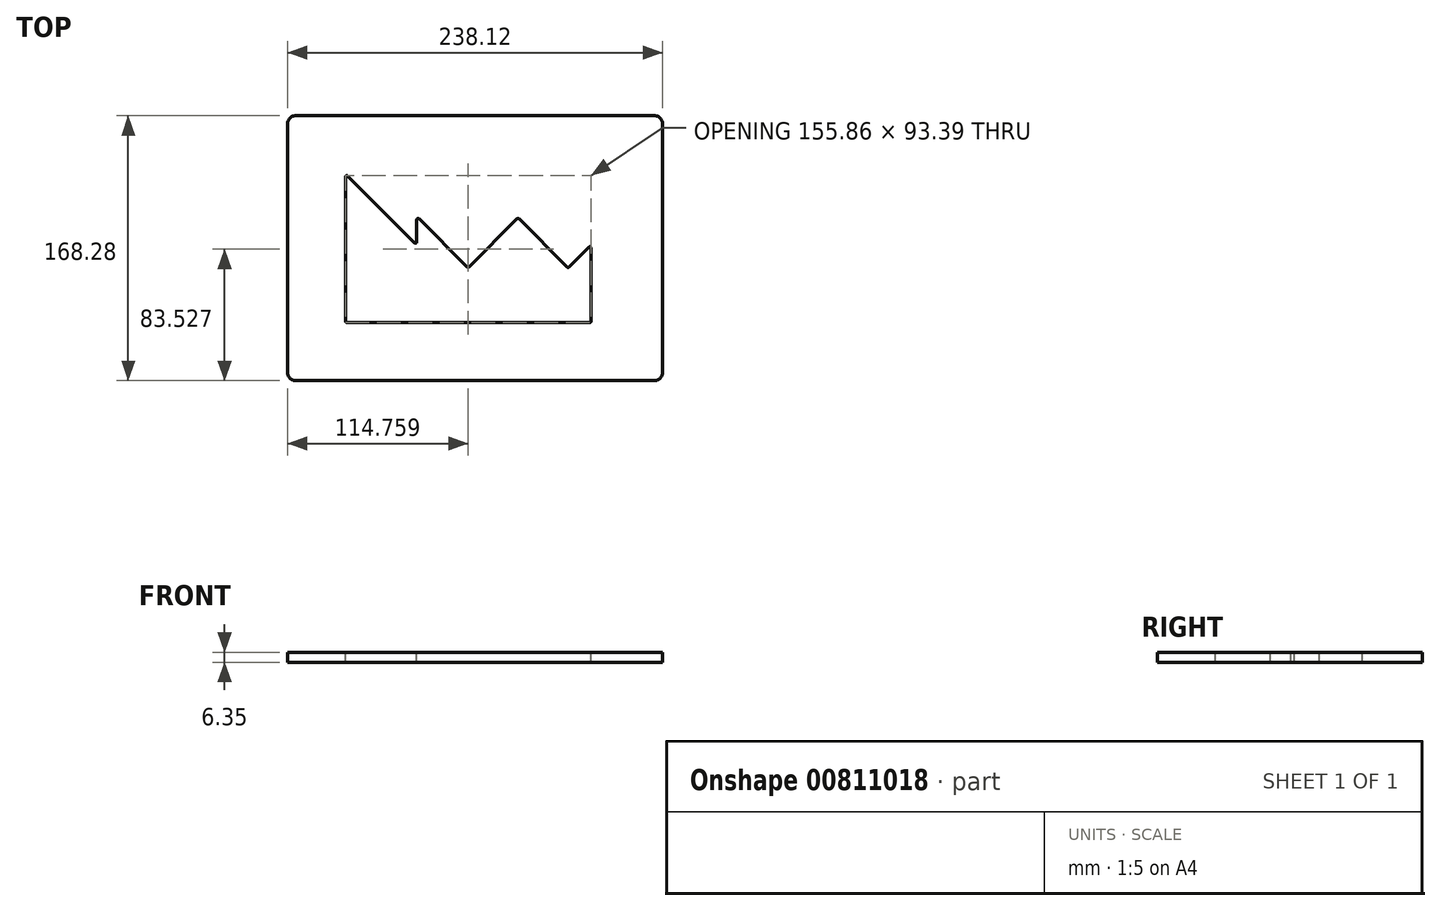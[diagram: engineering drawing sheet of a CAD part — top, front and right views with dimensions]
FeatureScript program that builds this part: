
annotation { "Feature Type Name" : "Feature", "Feature Type Description" : "" }
export const myFeature = defineFeature(function(context is Context, id is Id, definition is map)
    precondition{}
    {
        {
            var Q0;
            Q0=qCreatedBy(makeId("Top.planeOp"),FACE);
            var sketch = newSketch(context, id + "F0", { "sketchPlane" : qUnion([Q0])});
            skLineSegment(sketch, "E0.bottom", {"start": v(119.06, 84.14) * mm, "end": v(-119.06, 84.14) * mm});
            skLineSegment(sketch, "E0.top", {"start": v(119.06, -84.14) * mm, "end": v(-119.06, -84.14) * mm});
            skLineSegment(sketch, "E0.left", {"start": v(119.06, 84.14) * mm, "end": v(119.06, -84.14) * mm});
            skLineSegment(sketch, "E0.right", {"start": v(-119.06, 84.14) * mm, "end": v(-119.06, -84.14) * mm});
            skPoint(sketch, "E0.middle", {"position": v(0, 0) * mm});
            skSolve(sketch);
        }
        {
            var Q0;
            Q0 = qSketchRegion(id + "F0", true);
            extrude(context, id + "F1", {"entities" : qUnion([Q0]), "depth" : 6.35 * mm, "offsetDistance" : 25.4 * mm});
        }
        {
            var Q0;
            Q0=makeQuery(id+"F1.opExtrude","CAP_FACE",FACE,{"disambiguationData":[OSD([sQuery(id+"F0.wireOp",EDGE,"E0.bottom"),sQuery(id+"F0.wireOp",EDGE,"E0.top"),sQuery(id+"F0.wireOp",EDGE,"E0.left"),sQuery(id+"F0.wireOp",EDGE,"E0.right")])],"isStart":false});
            var sketch = newSketch(context, id + "F2", { "sketchPlane" : qUnion([Q0])});
            skLineSegment(sketch, "E1", {"start": v(-80.96, 44.13) * mm, "end": v(-80.96, -46.04) * mm});
            skLineSegment(sketch, "E2", {"start": v(-80.96, -46.04) * mm, "end": v(72.36, -46.04) * mm});
            skLineSegment(sketch, "E3", {"start": v(72.36, -46.04) * mm, "end": v(72.36, -1.08) * mm});
            skLineSegment(sketch, "E4", {"start": v(72.36, -1.08) * mm, "end": v(59.11, -14.33) * mm});
            skLineSegment(sketch, "E5", {"start": v(59.11, -14.33) * mm, "end": v(27.32, 17.46) * mm});
            skLineSegment(sketch, "E6", {"start": v(27.32, 17.46) * mm, "end": v(-4.47, -14.33) * mm});
            skLineSegment(sketch, "E7", {"start": v(-4.47, -14.33) * mm, "end": v(-35.75, 16.95) * mm});
            skLineSegment(sketch, "E8", {"start": v(-35.75, 16.95) * mm, "end": v(-35.75, -1.08) * mm});
            skLineSegment(sketch, "E9", {"start": v(-35.75, -1.08) * mm, "end": v(-80.96, 44.13) * mm});
            skSolve(sketch);
        }
        {
            var Q0;
            Q0 = qSketchRegion(id + "F2", true);
            extrude(context, id + "F3", {"entities" : qUnion([Q0]), "operationType" : NewBodyOperationType.REMOVE, "oppositeDirection" : true, "depth" : 25.4 * mm, "offsetDistance" : 25.4 * mm});
        }
        {
            var Q0;
            Q0=makeQuery(id+"F1.opExtrude","CAP_FACE",FACE,{"disambiguationData":[OSD([sQuery(id+"F0.wireOp",EDGE,"E0.bottom"),sQuery(id+"F0.wireOp",EDGE,"E0.top"),sQuery(id+"F0.wireOp",EDGE,"E0.left"),sQuery(id+"F0.wireOp",EDGE,"E0.right")])],"isStart":false});
            var sketch = newSketch(context, id + "F4", { "sketchPlane" : qUnion([Q0])});
            skLineSegment(sketch, "E10.0", {"start": v(-37.02, 18.12) * mm, "end": v(-37.02, 3.89) * mm});
            skLineSegment(sketch, "E10.1", {"start": v(-5.03, -11.97) * mm, "end": v(-35.68, 18.68) * mm});
            skLineSegment(sketch, "E10.2", {"start": v(-38.36, 3.33) * mm, "end": v(-80.89, 45.85) * mm});
            skLineSegment(sketch, "E10.3", {"start": v(26.76, 18.7) * mm, "end": v(-3.91, -11.97) * mm});
            skLineSegment(sketch, "E10.4", {"start": v(58.56, -11.97) * mm, "end": v(27.88, 18.7) * mm});
            skLineSegment(sketch, "E10.5", {"start": v(-82.23, 45.3) * mm, "end": v(-82.23, -46.52) * mm});
            skLineSegment(sketch, "E10.6", {"start": v(-81.45, -47.3) * mm, "end": v(72.84, -47.3) * mm});
            skLineSegment(sketch, "E10.7", {"start": v(73.63, -46.52) * mm, "end": v(73.63, 0.09) * mm});
            skLineSegment(sketch, "E10.8", {"start": v(72.29, 0.64) * mm, "end": v(59.67, -11.97) * mm});
            skPoint(sketch, "E11.visualSharp", {"position": v(-82.23, 47.2) * mm});
            skArc(sketch, "E11.filletArc", {"start": v(-80.89, 45.85) * mm, "mid": v(-81.75, 46.03) * mm, "end": v(-82.23, 45.3) * mm});
            skPoint(sketch, "E12.visualSharp", {"position": v(-37.02, 1.99) * mm});
            skArc(sketch, "E12.filletArc", {"start": v(-38.36, 3.33) * mm, "mid": v(-37.5, 3.16) * mm, "end": v(-37.02, 3.89) * mm});
            skPoint(sketch, "E13.visualSharp", {"position": v(-37.02, 20.02) * mm});
            skArc(sketch, "E13.filletArc", {"start": v(-35.68, 18.68) * mm, "mid": v(-36.53, 18.85) * mm, "end": v(-37.02, 18.12) * mm});
            skPoint(sketch, "E14.visualSharp", {"position": v(-4.47, -12.53) * mm});
            skArc(sketch, "E14.filletArc", {"start": v(-5.03, -11.97) * mm, "mid": v(-4.47, -12.2) * mm, "end": v(-3.91, -11.97) * mm});
            skPoint(sketch, "E15.visualSharp", {"position": v(27.32, 19.26) * mm});
            skArc(sketch, "E15.filletArc", {"start": v(27.88, 18.7) * mm, "mid": v(27.32, 18.93) * mm, "end": v(26.76, 18.7) * mm});
            skPoint(sketch, "E16.visualSharp", {"position": v(59.11, -12.53) * mm});
            skArc(sketch, "E16.filletArc", {"start": v(58.56, -11.97) * mm, "mid": v(59.11, -12.2) * mm, "end": v(59.67, -11.97) * mm});
            skPoint(sketch, "E17.visualSharp", {"position": v(73.63, 1.99) * mm});
            skArc(sketch, "E17.filletArc", {"start": v(73.63, 0.09) * mm, "mid": v(73.14, 0.81) * mm, "end": v(72.29, 0.64) * mm});
            skPoint(sketch, "E18.visualSharp", {"position": v(73.63, -47.3) * mm});
            skArc(sketch, "E18.filletArc", {"start": v(72.84, -47.3) * mm, "mid": v(73.4, -47.08) * mm, "end": v(73.63, -46.52) * mm});
            skPoint(sketch, "E19.visualSharp", {"position": v(-82.23, -47.3) * mm});
            skArc(sketch, "E19.filletArc", {"start": v(-82.23, -46.52) * mm, "mid": v(-82, -47.08) * mm, "end": v(-81.45, -47.3) * mm});
            skSolve(sketch);
        }
        {
            var Q0;
            Q0 = qSketchRegion(id + "F4", true);
            extrude(context, id + "F5", {"entities" : qUnion([Q0]), "operationType" : NewBodyOperationType.REMOVE, "oppositeDirection" : true, "depth" : 25.4 * mm, "offsetDistance" : 25.4 * mm});
        }
        {
            var Q0;
            Q0=makeQuery(id+"F1.opExtrude","SWEPT_EDGE",EDGE,{"disambiguationData":[OSD([sQuery(id+"F0.wireOp",EDGE,"E0.bottom"),sQuery(id+"F0.wireOp",EDGE,"E0.left")])]});
            var Q1;
            Q1=makeQuery(id+"F1.opExtrude","SWEPT_EDGE",EDGE,{"disambiguationData":[OSD([sQuery(id+"F0.wireOp",EDGE,"E0.top"),sQuery(id+"F0.wireOp",EDGE,"E0.left")])]});
            var Q2;
            Q2=makeQuery(id+"F1.opExtrude","SWEPT_EDGE",EDGE,{"disambiguationData":[OSD([sQuery(id+"F0.wireOp",EDGE,"E0.bottom"),sQuery(id+"F0.wireOp",EDGE,"E0.right")])]});
            var Q3;
            Q3=makeQuery(id+"F1.opExtrude","SWEPT_EDGE",EDGE,{"disambiguationData":[OSD([sQuery(id+"F0.wireOp",EDGE,"E0.top"),sQuery(id+"F0.wireOp",EDGE,"E0.right")])]});
            fillet(context, id + "F6", {"entities" : qUnion([Q0, Q1, Q2, Q3]), "radius" : 5.08 * mm, "tangentPropagation" : true, "allowEdgeOverflow" : false});
        }
    });
